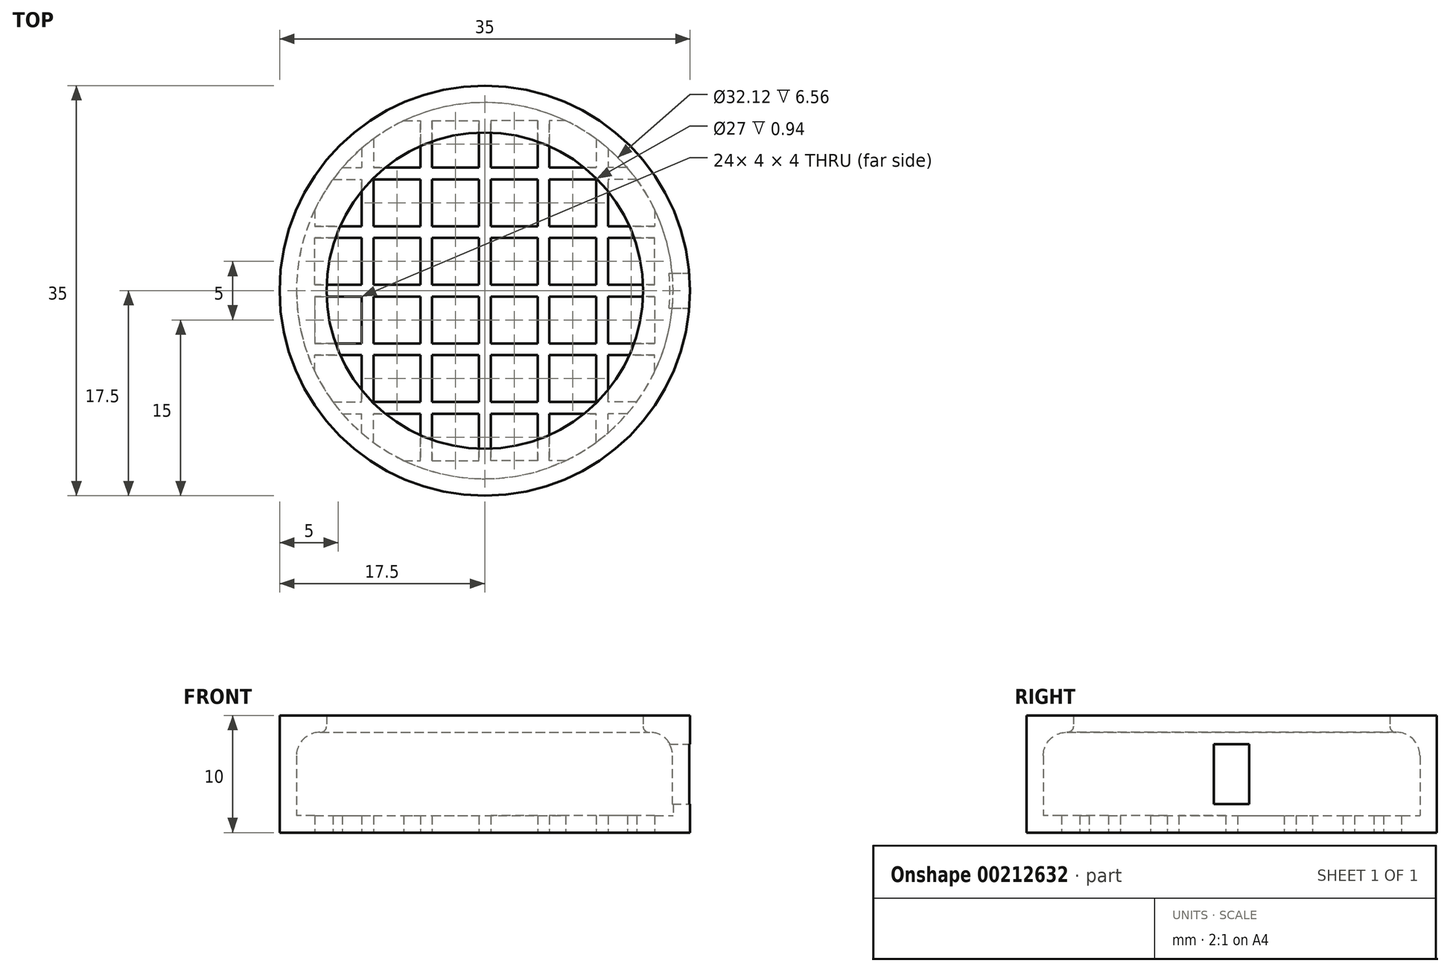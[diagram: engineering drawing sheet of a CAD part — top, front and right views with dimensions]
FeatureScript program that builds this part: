
annotation { "Feature Type Name" : "Feature", "Feature Type Description" : "" }
export const myFeature = defineFeature(function(context is Context, id is Id, definition is map)
    precondition{}
    {
        {
            var Q0;
            Q0=qCreatedBy(makeId("Front.planeOp"),FACE);
            var sketch = newSketch(context, id + "F0", { "sketchPlane" : qUnion([Q0])});
            skLineSegment(sketch, "E0", {"start": v(0, 0) * mm, "end": v(17.5, 0) * mm});
            skLineSegment(sketch, "E1", {"start": v(17.5, 0) * mm, "end": v(17.5, 10) * mm});
            skLineSegment(sketch, "E2", {"start": v(17.5, 10) * mm, "end": v(13.5, 10) * mm});
            skLineSegment(sketch, "E3.0", {"start": v(14.06, 8.56) * mm, "end": v(14, 8.56) * mm});
            skLineSegment(sketch, "E3.1", {"start": v(16.06, 1.44) * mm, "end": v(16.06, 6.56) * mm});
            skLineSegment(sketch, "E3.2", {"start": v(0, 1.44) * mm, "end": v(16.06, 1.44) * mm});
            skLineSegment(sketch, "E4", {"start": v(13.5, 9.06) * mm, "end": v(13.5, 10) * mm});
            skLineSegment(sketch, "E5", {"start": v(0, 0) * mm, "end": v(0, 1.44) * mm});
            skPoint(sketch, "E6.visualSharp", {"position": v(16.06, 8.56) * mm});
            skArc(sketch, "E6.filletArc", {"start": v(16.06, 6.56) * mm, "mid": v(15.47, 7.97) * mm, "end": v(14.06, 8.56) * mm});
            skPoint(sketch, "E7.visualSharp", {"position": v(13.5, 8.56) * mm});
            skArc(sketch, "E7.filletArc", {"start": v(13.5, 9.06) * mm, "mid": v(13.65, 8.7) * mm, "end": v(14, 8.56) * mm});
            skSolve(sketch);
        }
        {
            var Q0;
            Q0 = qSketchRegion(id + "F0", true);
            var Q1;
            Q1=sQuery(id+"F0.wireOp",EDGE,"E5");
            revolve(context, id + "F1", {"entities" : qUnion([Q0]), "axis" : qUnion([Q1]), "revolveType" : RevolveType.FULL});
        }
        {
            var Q0;
            Q0=makeQuery(id+"F1.opRevolve","SWEPT_FACE",FACE,{"disambiguationData":[OSD([sQuery(id+"F0.wireOp",EDGE,"E0")])]});
            var sketch = newSketch(context, id + "F2", { "sketchPlane" : qUnion([Q0])});
            skLineSegment(sketch, "E8.bottom", {"start": v(0.5, 4.5) * mm, "end": v(4.5, 4.5) * mm});
            skLineSegment(sketch, "E8.top", {"start": v(0.5, 0.5) * mm, "end": v(4.5, 0.5) * mm});
            skLineSegment(sketch, "E8.left", {"start": v(0.5, 4.5) * mm, "end": v(0.5, 0.5) * mm});
            skLineSegment(sketch, "E8.right", {"start": v(4.5, 4.5) * mm, "end": v(4.5, 0.5) * mm});
            skLineSegment(sketch, "E9.0.1.0", {"start": v(4.5, 9.5) * mm, "end": v(4.5, 5.5) * mm});
            skLineSegment(sketch, "E9.0.1.1", {"start": v(0.5, 9.5) * mm, "end": v(0.5, 5.5) * mm});
            skLineSegment(sketch, "E9.0.1.2", {"start": v(0.5, 5.5) * mm, "end": v(4.5, 5.5) * mm});
            skLineSegment(sketch, "E9.0.1.3", {"start": v(0.5, 9.5) * mm, "end": v(4.5, 9.5) * mm});
            skLineSegment(sketch, "E9.0.2.0", {"start": v(4.5, 14.5) * mm, "end": v(4.5, 10.5) * mm});
            skLineSegment(sketch, "E9.0.2.1", {"start": v(0.5, 14.5) * mm, "end": v(0.5, 10.5) * mm});
            skLineSegment(sketch, "E9.0.2.2", {"start": v(0.5, 10.5) * mm, "end": v(4.5, 10.5) * mm});
            skLineSegment(sketch, "E9.0.2.3", {"start": v(0.5, 14.5) * mm, "end": v(4.5, 14.5) * mm});
            skLineSegment(sketch, "E9.1.0.0", {"start": v(9.5, 4.5) * mm, "end": v(9.5, 0.5) * mm});
            skLineSegment(sketch, "E9.1.0.1", {"start": v(5.5, 4.5) * mm, "end": v(5.5, 0.5) * mm});
            skLineSegment(sketch, "E9.1.0.2", {"start": v(5.5, 0.5) * mm, "end": v(9.5, 0.5) * mm});
            skLineSegment(sketch, "E9.1.0.3", {"start": v(5.5, 4.5) * mm, "end": v(9.5, 4.5) * mm});
            skLineSegment(sketch, "E9.1.1.0", {"start": v(9.5, 9.5) * mm, "end": v(9.5, 5.5) * mm});
            skLineSegment(sketch, "E9.1.1.1", {"start": v(5.5, 9.5) * mm, "end": v(5.5, 5.5) * mm});
            skLineSegment(sketch, "E9.1.1.2", {"start": v(5.5, 5.5) * mm, "end": v(9.5, 5.5) * mm});
            skLineSegment(sketch, "E9.1.1.3", {"start": v(5.5, 9.5) * mm, "end": v(9.5, 9.5) * mm});
            skLineSegment(sketch, "E9.1.2.0", {"start": v(9.5, 14.5) * mm, "end": v(9.5, 10.5) * mm});
            skLineSegment(sketch, "E9.1.2.1", {"start": v(5.5, 14.5) * mm, "end": v(5.5, 10.5) * mm});
            skLineSegment(sketch, "E9.1.2.2", {"start": v(5.5, 10.5) * mm, "end": v(9.5, 10.5) * mm});
            skLineSegment(sketch, "E9.1.2.3", {"start": v(5.5, 14.5) * mm, "end": v(9.5, 14.5) * mm});
            skLineSegment(sketch, "E9.2.0.0", {"start": v(14.5, 4.5) * mm, "end": v(14.5, 0.5) * mm});
            skLineSegment(sketch, "E9.2.0.1", {"start": v(10.5, 4.5) * mm, "end": v(10.5, 0.5) * mm});
            skLineSegment(sketch, "E9.2.0.2", {"start": v(10.5, 0.5) * mm, "end": v(14.5, 0.5) * mm});
            skLineSegment(sketch, "E9.2.0.3", {"start": v(10.5, 4.5) * mm, "end": v(14.5, 4.5) * mm});
            skLineSegment(sketch, "E9.2.1.0", {"start": v(14.5, 9.5) * mm, "end": v(14.5, 5.5) * mm});
            skLineSegment(sketch, "E9.2.1.1", {"start": v(10.5, 9.5) * mm, "end": v(10.5, 5.5) * mm});
            skLineSegment(sketch, "E9.2.1.2", {"start": v(10.5, 5.5) * mm, "end": v(14.5, 5.5) * mm});
            skLineSegment(sketch, "E9.2.1.3", {"start": v(10.5, 9.5) * mm, "end": v(14.5, 9.5) * mm});
            skLineSegment(sketch, "E9.2.2.0", {"start": v(14.5, 14.5) * mm, "end": v(14.5, 10.5) * mm});
            skLineSegment(sketch, "E9.2.2.1", {"start": v(10.5, 14.5) * mm, "end": v(10.5, 10.5) * mm});
            skLineSegment(sketch, "E9.2.2.2", {"start": v(10.5, 10.5) * mm, "end": v(14.5, 10.5) * mm});
            skLineSegment(sketch, "E9.2.2.3", {"start": v(10.5, 14.5) * mm, "end": v(14.5, 14.5) * mm});
            skLineSegment(sketch, "E9.direction1", {"start": v(0.5, 0.5) * mm, "end": v(5.5, 0.5) * mm, "construction": true});
            skLineSegment(sketch, "E9.direction2", {"start": v(0.5, 0.5) * mm, "end": v(0.5, 5.5) * mm, "construction": true});
            skLineSegment(sketch, "E10.MirrorCS", {"start": v(-10.5, 4.5) * mm, "end": v(-10.5, 0.5) * mm});
            skLineSegment(sketch, "E11.MirrorCS", {"start": v(-0.5, 4.5) * mm, "end": v(-0.5, 0.5) * mm});
            skLineSegment(sketch, "E12.MirrorCS", {"start": v(-0.5, 0.5) * mm, "end": v(-4.5, 0.5) * mm});
            skLineSegment(sketch, "E13.MirrorCS", {"start": v(-9.5, 9.5) * mm, "end": v(-9.5, 5.5) * mm});
            skLineSegment(sketch, "E14.MirrorCS", {"start": v(-5.5, 14.5) * mm, "end": v(-5.5, 10.5) * mm});
            skLineSegment(sketch, "E15.MirrorCS", {"start": v(-14.5, 9.5) * mm, "end": v(-14.5, 5.5) * mm});
            skLineSegment(sketch, "E16.MirrorCS", {"start": v(-0.5, 0.5) * mm, "end": v(-0.5, 5.5) * mm, "construction": true});
            skLineSegment(sketch, "E17.MirrorCS", {"start": v(-0.5, 0.5) * mm, "end": v(-5.5, 0.5) * mm, "construction": true});
            skLineSegment(sketch, "E18.MirrorCS", {"start": v(-5.5, 4.5) * mm, "end": v(-9.5, 4.5) * mm});
            skLineSegment(sketch, "E19.MirrorCS", {"start": v(-10.5, 4.5) * mm, "end": v(-14.5, 4.5) * mm});
            skLineSegment(sketch, "E20.MirrorCS", {"start": v(-14.5, 14.5) * mm, "end": v(-14.5, 10.5) * mm});
            skLineSegment(sketch, "E21.MirrorCS", {"start": v(-5.5, 0.5) * mm, "end": v(-9.5, 0.5) * mm});
            skLineSegment(sketch, "E22.MirrorCS", {"start": v(-5.5, 4.5) * mm, "end": v(-5.5, 0.5) * mm});
            skLineSegment(sketch, "E23.MirrorCS", {"start": v(-10.5, 0.5) * mm, "end": v(-14.5, 0.5) * mm});
            skLineSegment(sketch, "E24.MirrorCS", {"start": v(-9.5, 14.5) * mm, "end": v(-9.5, 10.5) * mm});
            skLineSegment(sketch, "E25.MirrorCS", {"start": v(-9.5, 4.5) * mm, "end": v(-9.5, 0.5) * mm});
            skLineSegment(sketch, "E26.MirrorCS", {"start": v(-14.5, 4.5) * mm, "end": v(-14.5, 0.5) * mm});
            skLineSegment(sketch, "E27.MirrorCS", {"start": v(-10.5, 10.5) * mm, "end": v(-14.5, 10.5) * mm});
            skLineSegment(sketch, "E28.MirrorCS", {"start": v(-5.5, 10.5) * mm, "end": v(-9.5, 10.5) * mm});
            skLineSegment(sketch, "E29.MirrorCS", {"start": v(-10.5, 9.5) * mm, "end": v(-10.5, 5.5) * mm});
            skLineSegment(sketch, "E30.MirrorCS", {"start": v(-5.5, 9.5) * mm, "end": v(-5.5, 5.5) * mm});
            skLineSegment(sketch, "E31.MirrorCS", {"start": v(-10.5, 14.5) * mm, "end": v(-14.5, 14.5) * mm});
            skLineSegment(sketch, "E32.MirrorCS", {"start": v(-5.5, 14.5) * mm, "end": v(-9.5, 14.5) * mm});
            skLineSegment(sketch, "E33.MirrorCS", {"start": v(-10.5, 9.5) * mm, "end": v(-14.5, 9.5) * mm});
            skLineSegment(sketch, "E34.MirrorCS", {"start": v(-10.5, 5.5) * mm, "end": v(-14.5, 5.5) * mm});
            skLineSegment(sketch, "E35.MirrorCS", {"start": v(-5.5, 9.5) * mm, "end": v(-9.5, 9.5) * mm});
            skLineSegment(sketch, "E36.MirrorCS", {"start": v(-5.5, 5.5) * mm, "end": v(-9.5, 5.5) * mm});
            skLineSegment(sketch, "E37.MirrorCS", {"start": v(-4.5, 9.5) * mm, "end": v(-4.5, 5.5) * mm});
            skLineSegment(sketch, "E38.MirrorCS", {"start": v(-0.5, 9.5) * mm, "end": v(-0.5, 5.5) * mm});
            skLineSegment(sketch, "E39.MirrorCS", {"start": v(-4.5, 14.5) * mm, "end": v(-4.5, 10.5) * mm});
            skLineSegment(sketch, "E40.MirrorCS", {"start": v(-0.5, 9.5) * mm, "end": v(-4.5, 9.5) * mm});
            skLineSegment(sketch, "E41.MirrorCS", {"start": v(-10.5, 14.5) * mm, "end": v(-10.5, 10.5) * mm});
            skLineSegment(sketch, "E42.MirrorCS", {"start": v(-0.5, 5.5) * mm, "end": v(-4.5, 5.5) * mm});
            skLineSegment(sketch, "E43.MirrorCS", {"start": v(-4.5, 4.5) * mm, "end": v(-4.5, 0.5) * mm});
            skLineSegment(sketch, "E44.MirrorCS", {"start": v(-0.5, 10.5) * mm, "end": v(-4.5, 10.5) * mm});
            skLineSegment(sketch, "E45.MirrorCS", {"start": v(-0.5, 14.5) * mm, "end": v(-0.5, 10.5) * mm});
            skLineSegment(sketch, "E46.MirrorCS", {"start": v(-0.5, 14.5) * mm, "end": v(-4.5, 14.5) * mm});
            skLineSegment(sketch, "E47.MirrorCS", {"start": v(-0.5, 4.5) * mm, "end": v(-4.5, 4.5) * mm});
            skLineSegment(sketch, "E48.MirrorCS", {"start": v(0.5, -4.5) * mm, "end": v(0.5, -0.5) * mm});
            skLineSegment(sketch, "E49.MirrorCS", {"start": v(10.5, -4.5) * mm, "end": v(10.5, -0.5) * mm});
            skLineSegment(sketch, "E50.MirrorCS", {"start": v(-0.5, -4.5) * mm, "end": v(-0.5, -0.5) * mm});
            skLineSegment(sketch, "E51.MirrorCS", {"start": v(0.5, -0.5) * mm, "end": v(4.5, -0.5) * mm});
            skLineSegment(sketch, "E52.MirrorCS", {"start": v(-0.5, -0.5) * mm, "end": v(-4.5, -0.5) * mm});
            skLineSegment(sketch, "E53.MirrorCS", {"start": v(-10.5, -9.5) * mm, "end": v(-10.5, -5.5) * mm});
            skLineSegment(sketch, "E54.MirrorCS", {"start": v(-0.5, -14.5) * mm, "end": v(-4.5, -14.5) * mm});
            skLineSegment(sketch, "E55.MirrorCS", {"start": v(10.5, -10.5) * mm, "end": v(14.5, -10.5) * mm});
            skLineSegment(sketch, "E56.MirrorCS", {"start": v(5.5, -10.5) * mm, "end": v(9.5, -10.5) * mm});
            skLineSegment(sketch, "E57.MirrorCS", {"start": v(5.5, -5.5) * mm, "end": v(9.5, -5.5) * mm});
            skLineSegment(sketch, "E58.MirrorCS", {"start": v(10.5, -5.5) * mm, "end": v(14.5, -5.5) * mm});
            skLineSegment(sketch, "E59.MirrorCS", {"start": v(-14.5, -4.5) * mm, "end": v(-14.5, -0.5) * mm});
            skLineSegment(sketch, "E60.MirrorCS", {"start": v(-4.5, -4.5) * mm, "end": v(-4.5, -0.5) * mm});
            skLineSegment(sketch, "E61.MirrorCS", {"start": v(-5.5, -4.5) * mm, "end": v(-9.5, -4.5) * mm});
            skLineSegment(sketch, "E62.MirrorCS", {"start": v(-10.5, -9.5) * mm, "end": v(-14.5, -9.5) * mm});
            skLineSegment(sketch, "E63.MirrorCS", {"start": v(-0.5, -5.5) * mm, "end": v(-4.5, -5.5) * mm});
            skLineSegment(sketch, "E64.MirrorCS", {"start": v(-5.5, -14.5) * mm, "end": v(-5.5, -10.5) * mm});
            skLineSegment(sketch, "E65.MirrorCS", {"start": v(-5.5, -14.5) * mm, "end": v(-9.5, -14.5) * mm});
            skLineSegment(sketch, "E66.MirrorCS", {"start": v(0.5, -0.5) * mm, "end": v(5.5, -0.5) * mm, "construction": true});
            skLineSegment(sketch, "E67.MirrorCS", {"start": v(-0.5, -14.5) * mm, "end": v(-0.5, -10.5) * mm});
            skLineSegment(sketch, "E68.MirrorCS", {"start": v(-10.5, -4.5) * mm, "end": v(-10.5, -0.5) * mm});
            skLineSegment(sketch, "E69.MirrorCS", {"start": v(-10.5, -4.5) * mm, "end": v(-14.5, -4.5) * mm});
            skLineSegment(sketch, "E70.MirrorCS", {"start": v(-4.5, -14.5) * mm, "end": v(-4.5, -10.5) * mm});
            skLineSegment(sketch, "E71.MirrorCS", {"start": v(-0.5, -4.5) * mm, "end": v(-4.5, -4.5) * mm});
            skLineSegment(sketch, "E72.MirrorCS", {"start": v(5.5, -4.5) * mm, "end": v(5.5, -0.5) * mm});
            skLineSegment(sketch, "E73.MirrorCS", {"start": v(-5.5, -5.5) * mm, "end": v(-9.5, -5.5) * mm});
            skLineSegment(sketch, "E74.MirrorCS", {"start": v(-5.5, -0.5) * mm, "end": v(-9.5, -0.5) * mm});
            skLineSegment(sketch, "E75.MirrorCS", {"start": v(14.5, -9.5) * mm, "end": v(14.5, -5.5) * mm});
            skLineSegment(sketch, "E76.MirrorCS", {"start": v(9.5, -9.5) * mm, "end": v(9.5, -5.5) * mm});
            skLineSegment(sketch, "E77.MirrorCS", {"start": v(-0.5, -9.5) * mm, "end": v(-0.5, -5.5) * mm});
            skLineSegment(sketch, "E78.MirrorCS", {"start": v(0.5, -0.5) * mm, "end": v(0.5, -5.5) * mm, "construction": true});
            skLineSegment(sketch, "E79.MirrorCS", {"start": v(10.5, -9.5) * mm, "end": v(10.5, -5.5) * mm});
            skLineSegment(sketch, "E80.MirrorCS", {"start": v(5.5, -9.5) * mm, "end": v(5.5, -5.5) * mm});
            skLineSegment(sketch, "E81.MirrorCS", {"start": v(10.5, -14.5) * mm, "end": v(14.5, -14.5) * mm});
            skLineSegment(sketch, "E82.MirrorCS", {"start": v(5.5, -14.5) * mm, "end": v(9.5, -14.5) * mm});
            skLineSegment(sketch, "E83.MirrorCS", {"start": v(9.5, -4.5) * mm, "end": v(9.5, -0.5) * mm});
            skLineSegment(sketch, "E84.MirrorCS", {"start": v(14.5, -4.5) * mm, "end": v(14.5, -0.5) * mm});
            skLineSegment(sketch, "E85.MirrorCS", {"start": v(-5.5, -9.5) * mm, "end": v(-9.5, -9.5) * mm});
            skLineSegment(sketch, "E86.MirrorCS", {"start": v(10.5, -9.5) * mm, "end": v(14.5, -9.5) * mm});
            skLineSegment(sketch, "E87.MirrorCS", {"start": v(10.5, -14.5) * mm, "end": v(10.5, -10.5) * mm});
            skLineSegment(sketch, "E88.MirrorCS", {"start": v(5.5, -9.5) * mm, "end": v(9.5, -9.5) * mm});
            skLineSegment(sketch, "E89.MirrorCS", {"start": v(0.5, -14.5) * mm, "end": v(4.5, -14.5) * mm});
            skLineSegment(sketch, "E90.MirrorCS", {"start": v(4.5, -14.5) * mm, "end": v(4.5, -10.5) * mm});
            skLineSegment(sketch, "E91.MirrorCS", {"start": v(0.5, -14.5) * mm, "end": v(0.5, -10.5) * mm});
            skLineSegment(sketch, "E92.MirrorCS", {"start": v(0.5, -10.5) * mm, "end": v(4.5, -10.5) * mm});
            skLineSegment(sketch, "E93.MirrorCS", {"start": v(0.5, -9.5) * mm, "end": v(4.5, -9.5) * mm});
            skLineSegment(sketch, "E94.MirrorCS", {"start": v(0.5, -5.5) * mm, "end": v(4.5, -5.5) * mm});
            skLineSegment(sketch, "E95.MirrorCS", {"start": v(-0.5, -0.5) * mm, "end": v(-5.5, -0.5) * mm, "construction": true});
            skLineSegment(sketch, "E96.MirrorCS", {"start": v(-0.5, -0.5) * mm, "end": v(-0.5, -5.5) * mm, "construction": true});
            skLineSegment(sketch, "E97.MirrorCS", {"start": v(-0.5, -9.5) * mm, "end": v(-4.5, -9.5) * mm});
            skLineSegment(sketch, "E98.MirrorCS", {"start": v(-14.5, -14.5) * mm, "end": v(-14.5, -10.5) * mm});
            skLineSegment(sketch, "E99.MirrorCS", {"start": v(-0.5, -10.5) * mm, "end": v(-4.5, -10.5) * mm});
            skLineSegment(sketch, "E100.MirrorCS", {"start": v(-10.5, -10.5) * mm, "end": v(-14.5, -10.5) * mm});
            skLineSegment(sketch, "E101.MirrorCS", {"start": v(-5.5, -10.5) * mm, "end": v(-9.5, -10.5) * mm});
            skLineSegment(sketch, "E102.MirrorCS", {"start": v(-10.5, -14.5) * mm, "end": v(-10.5, -10.5) * mm});
            skLineSegment(sketch, "E103.MirrorCS", {"start": v(-5.5, -9.5) * mm, "end": v(-5.5, -5.5) * mm});
            skLineSegment(sketch, "E104.MirrorCS", {"start": v(-9.5, -4.5) * mm, "end": v(-9.5, -0.5) * mm});
            skLineSegment(sketch, "E105.MirrorCS", {"start": v(-9.5, -14.5) * mm, "end": v(-9.5, -10.5) * mm});
            skLineSegment(sketch, "E106.MirrorCS", {"start": v(9.5, -14.5) * mm, "end": v(9.5, -10.5) * mm});
            skLineSegment(sketch, "E107.MirrorCS", {"start": v(5.5, -4.5) * mm, "end": v(9.5, -4.5) * mm});
            skLineSegment(sketch, "E108.MirrorCS", {"start": v(5.5, -0.5) * mm, "end": v(9.5, -0.5) * mm});
            skLineSegment(sketch, "E109.MirrorCS", {"start": v(5.5, -14.5) * mm, "end": v(5.5, -10.5) * mm});
            skLineSegment(sketch, "E110.MirrorCS", {"start": v(10.5, -4.5) * mm, "end": v(14.5, -4.5) * mm});
            skLineSegment(sketch, "E111.MirrorCS", {"start": v(10.5, -0.5) * mm, "end": v(14.5, -0.5) * mm});
            skLineSegment(sketch, "E112.MirrorCS", {"start": v(14.5, -14.5) * mm, "end": v(14.5, -10.5) * mm});
            skLineSegment(sketch, "E113.MirrorCS", {"start": v(-14.5, -9.5) * mm, "end": v(-14.5, -5.5) * mm});
            skLineSegment(sketch, "E114.MirrorCS", {"start": v(-5.5, -4.5) * mm, "end": v(-5.5, -0.5) * mm});
            skLineSegment(sketch, "E115.MirrorCS", {"start": v(-4.5, -9.5) * mm, "end": v(-4.5, -5.5) * mm});
            skLineSegment(sketch, "E116.MirrorCS", {"start": v(-9.5, -9.5) * mm, "end": v(-9.5, -5.5) * mm});
            skLineSegment(sketch, "E117.MirrorCS", {"start": v(4.5, -4.5) * mm, "end": v(4.5, -0.5) * mm});
            skLineSegment(sketch, "E118.MirrorCS", {"start": v(-10.5, -0.5) * mm, "end": v(-14.5, -0.5) * mm});
            skLineSegment(sketch, "E119.MirrorCS", {"start": v(-10.5, -14.5) * mm, "end": v(-14.5, -14.5) * mm});
            skLineSegment(sketch, "E120.MirrorCS", {"start": v(-10.5, -5.5) * mm, "end": v(-14.5, -5.5) * mm});
            skLineSegment(sketch, "E121.MirrorCS", {"start": v(4.5, -9.5) * mm, "end": v(4.5, -5.5) * mm});
            skLineSegment(sketch, "E122.MirrorCS", {"start": v(0.5, -9.5) * mm, "end": v(0.5, -5.5) * mm});
            skLineSegment(sketch, "E123.MirrorCS", {"start": v(0.5, -4.5) * mm, "end": v(4.5, -4.5) * mm});
            skSolve(sketch);
        }
        {
            var Q0;
            Q0 = qSketchRegion(id + "F2", true);
            var Q1;
            Q1=makeQuery(id+"F1.opRevolve","SWEPT_FACE",FACE,{"disambiguationData":[OSD([sQuery(id+"F0.wireOp",EDGE,"E3.2")])]});
            extrude(context, id + "F3", {"entities" : qUnion([Q0]), "operationType" : NewBodyOperationType.REMOVE, "endBound" : BoundingType.UP_TO_SURFACE, "oppositeDirection" : true, "endBoundEntityFace" : qUnion([Q1]), "depth" : 25 * mm});
        }
        {
            var Q0;
            Q0=makeQuery(id+"F1.opRevolve","SWEPT_FACE",FACE,{"disambiguationData":[OSD([sQuery(id+"F0.wireOp",EDGE,"E0")])]});
            var sketch = newSketch(context, id + "F4", { "sketchPlane" : qUnion([Q0])});
            skCircle(sketch, "E124", {"center": v(0, 0) * mm, "radius": 17.5 * mm});
            skCircle(sketch, "E125", {"center": v(0, 0) * mm, "radius": 16.06 * mm});
            skSolve(sketch);
        }
        {
            var Q0;
            Q0 = qSketchRegion(id + "F4", true);
            var Q1;
            Q1=makeQuery(id+"F1.opRevolve","SWEPT_FACE",FACE,{"disambiguationData":[OSD([sQuery(id+"F0.wireOp",EDGE,"E3.2")])]});
            extrude(context, id + "F5", {"entities" : qUnion([Q0]), "operationType" : NewBodyOperationType.ADD, "endBound" : BoundingType.UP_TO_SURFACE, "oppositeDirection" : true, "endBoundEntityFace" : qUnion([Q1]), "depth" : 25 * mm});
        }
        {
            var Q0;
            Q0=qCreatedBy(makeId("Front.planeOp"),FACE);
            var sketch = newSketch(context, id + "F6", { "sketchPlane" : qUnion([Q0])});
            skLineSegment(sketch, "E126.bottom", {"start": v(13.5, 7.56) * mm, "end": v(17.5, 7.56) * mm});
            skLineSegment(sketch, "E126.top", {"start": v(13.5, 2.44) * mm, "end": v(17.5, 2.44) * mm});
            skLineSegment(sketch, "E126.left", {"start": v(13.5, 7.56) * mm, "end": v(13.5, 2.44) * mm});
            skLineSegment(sketch, "E126.right", {"start": v(17.5, 7.56) * mm, "end": v(17.5, 2.44) * mm});
            skSolve(sketch);
        }
        {
            var Q0;
            Q0 = qSketchRegion(id + "F6", true);
            extrude(context, id + "F7", {"entities" : qUnion([Q0]), "operationType" : NewBodyOperationType.REMOVE, "endBound" : BoundingType.SYMMETRIC, "depth" : 3 * mm});
        }
    });
